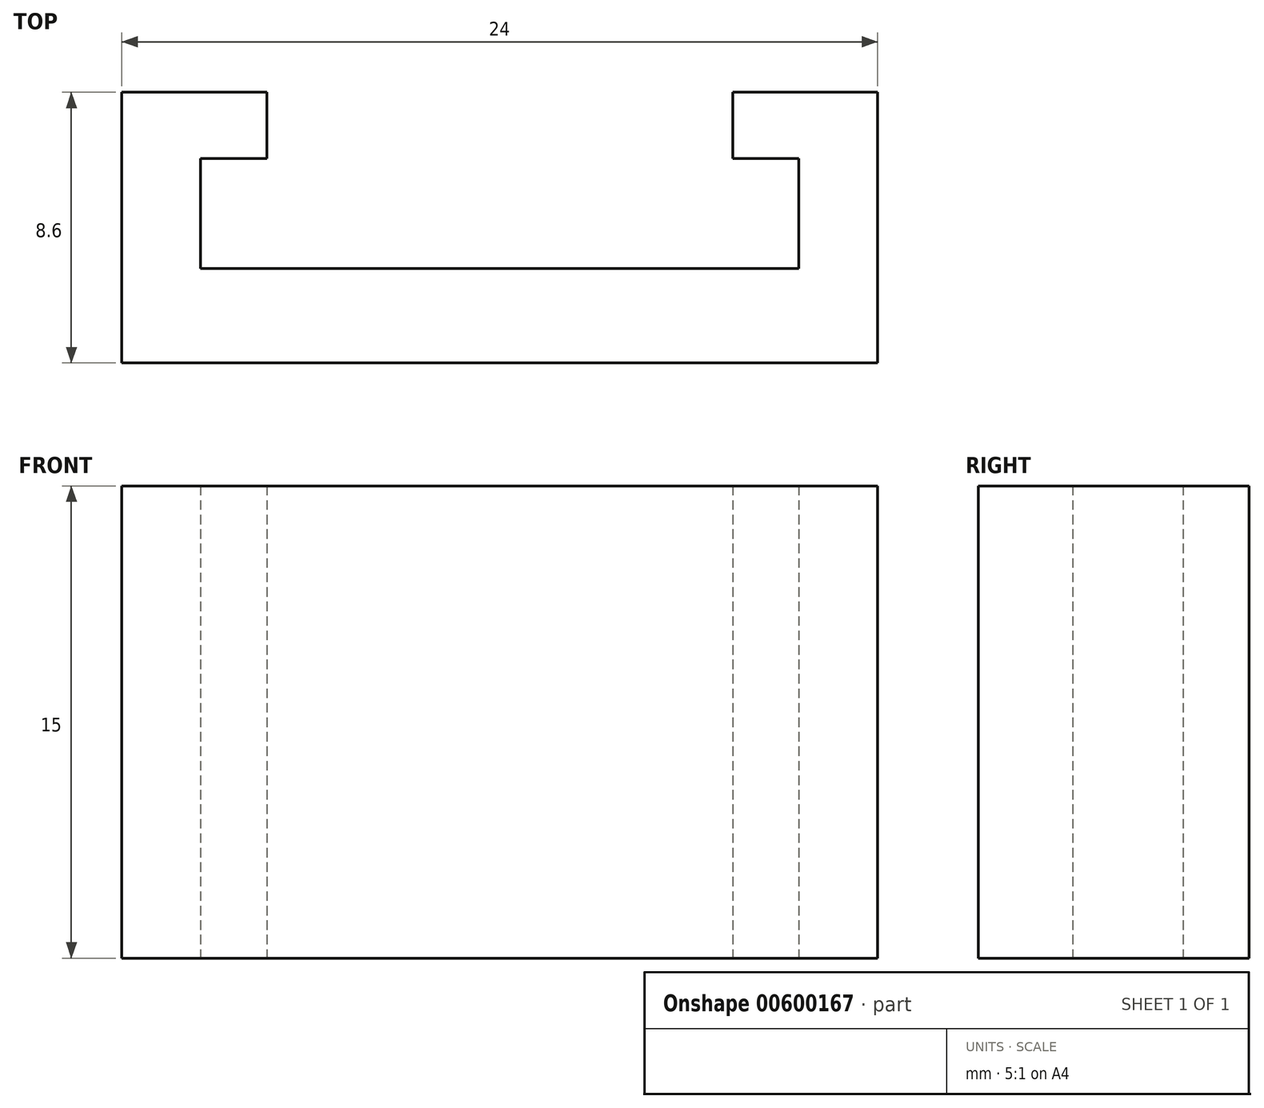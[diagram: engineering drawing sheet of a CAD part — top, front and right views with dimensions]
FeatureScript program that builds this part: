
annotation { "Feature Type Name" : "Feature", "Feature Type Description" : "" }
export const myFeature = defineFeature(function(context is Context, id is Id, definition is map)
    precondition{}
    {
        {
            var Q0;
            Q0=qCreatedBy(makeId("Top.planeOp"),FACE);
            var sketch = newSketch(context, id + "F0", { "sketchPlane" : qUnion([Q0])});
            skLineSegment(sketch, "E0", {"start": v(0, 0) * mm, "end": v(-11, 0) * mm});
            skLineSegment(sketch, "E1", {"start": v(0, 0) * mm, "end": v(0, 3) * mm});
            skLineSegment(sketch, "E2", {"start": v(0, 3) * mm, "end": v(-4, 3) * mm});
            skLineSegment(sketch, "E3", {"start": v(-9.5, 3) * mm, "end": v(-9.5, 6.5) * mm});
            skLineSegment(sketch, "E4", {"start": v(-9.5, 6.5) * mm, "end": v(-7.4, 6.5) * mm});
            skLineSegment(sketch, "E5", {"start": v(-7.4, 6.5) * mm, "end": v(-7.4, 8.6) * mm});
            skLineSegment(sketch, "E6", {"start": v(-7.4, 8.6) * mm, "end": v(-11, 8.6) * mm});
            skPoint(sketch, "E7.end.orphan", {"position": v(-6, 3) * mm});
            skLineSegment(sketch, "E8.trimOffspring", {"start": v(-6, 3) * mm, "end": v(-9.5, 3) * mm});
            skLineSegment(sketch, "E9", {"start": v(-4, 3) * mm, "end": v(-6, 3) * mm});
            skLineSegment(sketch, "E10", {"start": v(-11, 0) * mm, "end": v(-12, 0) * mm});
            skLineSegment(sketch, "E11", {"start": v(-12, 0) * mm, "end": v(-12, 8.6) * mm});
            skLineSegment(sketch, "E12", {"start": v(-12, 8.6) * mm, "end": v(-11, 8.6) * mm});
            skPoint(sketch, "E13.end.orphan", {"position": v(-11, 0) * mm});
            skSolve(sketch);
        }
        {
            var Q0;
            Q0=makeQuery(id+"F0.imprint","IMPRINT",FACE,{"disambiguationData":[TD([[makeQuery(id+"F0.imprint","IMPRINT",EDGE,{"derivedFrom":sQuery(id+"F0.wireOp",EDGE,"E0")}),-1.0]])]});
            extrude(context, id + "F1", {"entities" : qUnion([Q0]), "depth" : 15 * mm, "offsetDistance" : 25 * mm});
        }
        {
            var Q0;
            Q0=makeQuery(id+"F1.opExtrude","SWEPT_BODY",BODY,{"disambiguationData":[OSD([sQuery(id+"F0.wireOp",EDGE,"E0"),sQuery(id+"F0.wireOp",EDGE,"E1"),sQuery(id+"F0.wireOp",EDGE,"E2"),sQuery(id+"F0.wireOp",EDGE,"E3"),sQuery(id+"F0.wireOp",EDGE,"E4"),sQuery(id+"F0.wireOp",EDGE,"E5"),sQuery(id+"F0.wireOp",EDGE,"E6"),sQuery(id+"F0.wireOp",EDGE,"E13")])]});
            var Q1;
            Q1=qCreatedBy(makeId("Right.planeOp"),FACE);
            mirror(context, id + "F2", {"operationType" : NewBodyOperationType.ADD, "entities" : qUnion([Q0]), "mirrorPlane" : qUnion([Q1])});
        }
    });
